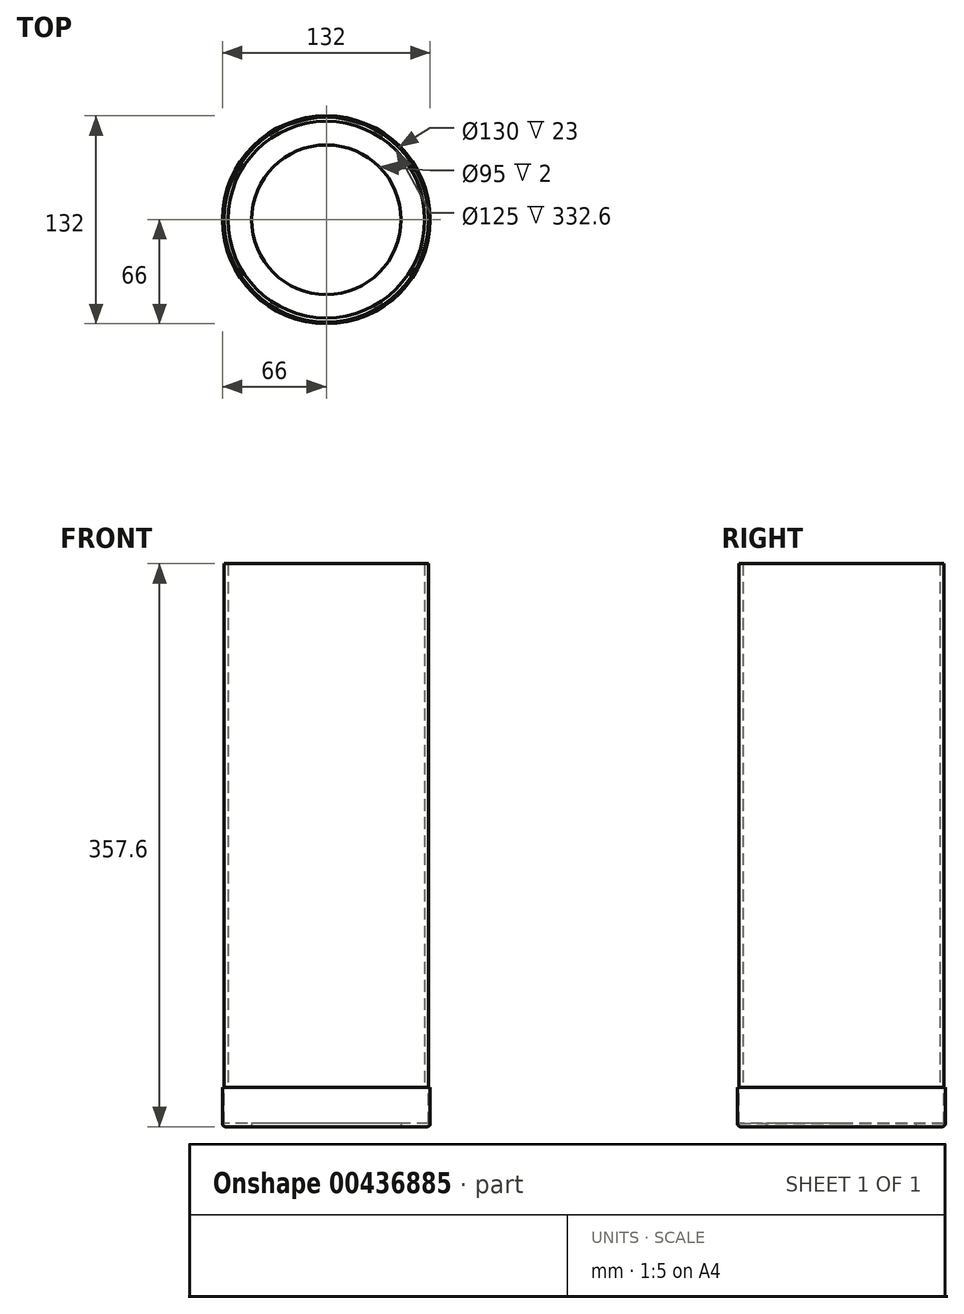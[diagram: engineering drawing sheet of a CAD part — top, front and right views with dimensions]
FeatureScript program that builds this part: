
annotation { "Feature Type Name" : "Feature", "Feature Type Description" : "" }
export const myFeature = defineFeature(function(context is Context, id is Id, definition is map)
    precondition{}
    {
        {
            var Q0;
            Q0=qCreatedBy(makeId("Top.planeOp"),FACE);
            var sketch = newSketch(context, id + "F0", { "sketchPlane" : qUnion([Q0])});
            skCircle(sketch, "E0", {"center": v(0, 0) * mm, "radius": 65 * mm});
            skSolve(sketch);
        }
        {
            var Q0;
            Q0=makeQuery(id+"F0.imprint","IMPRINT",FACE,{"disambiguationData":[TD([[makeQuery(id+"F0.imprint","IMPRINT",EDGE,{"derivedFrom":sQuery(id+"F0.wireOp",EDGE,"E0")}),1.0]])]});
            extrude(context, id + "F1", {"entities" : qUnion([Q0]), "depth" : 355.6 * mm});
        }
        {
            var Q0;
            Q0=makeQuery(id+"F1.opExtrude","CAP_FACE",FACE,{"disambiguationData":[OSD([sQuery(id+"F0.wireOp",EDGE,"E0")])],"isStart":false});
            shell(context, id + "F2", {"entities" : qUnion([Q0]), "thickness" : 2.5 * mm});
        }
        {
            var Q0;
            {var subQ0=sQuery(id+"F0.wireOp",EDGE,"E0");Q0=makeQuery(id+"F2.opShell","OFFSET_FACE",FACE,{"disambiguationData":[OSD([subQ0]),TDD([makeQuery(id+"F1.opExtrude","CAP_FACE",FACE,{"disambiguationData":[OSD([subQ0])],"isStart":true})])]});}
            extrude(context, id + "F3", {"entities" : qUnion([Q0]), "operationType" : NewBodyOperationType.REMOVE, "oppositeDirection" : true, "depth" : 25 * mm});
        }
        {
            var Q0;
            Q0=qCreatedBy(makeId("Top.planeOp"),FACE);
            cPlane(context, id + "F4", {"entities" : qUnion([Q0]), "cplaneType" : CPlaneType.OFFSET, "offset" : 2 * mm, "oppositeDirection" : true, "width" : 150 * mm, "height" : 150 * mm});
        }
        {
            var Q0;
            Q0=qCreatedBy(id+"F4.planeOp",FACE);
            var sketch = newSketch(context, id + "F5", { "sketchPlane" : qUnion([Q0])});
            skCircle(sketch, "E1", {"center": v(0, 0) * mm, "radius": 66 * mm});
            skSolve(sketch);
        }
        {
            var Q0;
            Q0=makeQuery(id+"F5.imprint","IMPRINT",FACE,{"disambiguationData":[TD([[makeQuery(id+"F5.imprint","IMPRINT",EDGE,{"derivedFrom":sQuery(id+"F5.wireOp",EDGE,"E1")}),1.0]])]});
            extrude(context, id + "F6", {"entities" : qUnion([Q0]), "depth" : 25 * mm});
        }
        {
            var Q0;
            Q0=makeQuery(id+"F6.opExtrude","CAP_FACE",FACE,{"disambiguationData":[OSD([sQuery(id+"F5.wireOp",EDGE,"E1")])],"isStart":false});
            var sketch = newSketch(context, id + "F7", { "sketchPlane" : qUnion([Q0])});
            skCircle(sketch, "E2", {"center": v(0, 0) * mm, "radius": 65 * mm});
            skSolve(sketch);
        }
        {
            var Q0;
            Q0=makeQuery(id+"F7.imprint","IMPRINT",FACE,{"disambiguationData":[TD([[makeQuery(id+"F7.imprint","IMPRINT",EDGE,{"derivedFrom":sQuery(id+"F7.wireOp",EDGE,"E2")}),1.0]])]});
            extrude(context, id + "F8", {"entities" : qUnion([Q0]), "operationType" : NewBodyOperationType.REMOVE, "oppositeDirection" : true, "depth" : 23 * mm});
        }
        {
            var Q0;
            Q0=makeQuery(id+"F6.opExtrude","CAP_EDGE",EDGE,{"disambiguationData":[OSD([sQuery(id+"F5.wireOp",EDGE,"E1")])],"isStart":true});
            fillet(context, id + "F9", {"entities" : qUnion([Q0]), "radius" : 2 * mm, "tangentPropagation" : true, "allowEdgeOverflow" : false});
        }
        {
            var Q0;
            Q0=makeQuery(id+"F6.opExtrude","CAP_FACE",FACE,{"disambiguationData":[OSD([sQuery(id+"F5.wireOp",EDGE,"E1")])],"isStart":true});
            var sketch = newSketch(context, id + "F10", { "sketchPlane" : qUnion([Q0])});
            skPoint(sketch, "E3", {"position": v(0, 0) * mm});
            skSolve(sketch);
        }
        {
            var Q0;
            Q0=sQuery(id+"F10.wireOp",VERTEX,"E3");
            var Q1;
            Q1=makeQuery(id+"F6.opExtrude","SWEPT_BODY",BODY,{"disambiguationData":[OSD([sQuery(id+"F5.wireOp",EDGE,"E1")])]});
            hole(context, id + "F11", {"style" : HoleStyle.SIMPLE, "endStyle" : HoleEndStyle.BLIND, "holeDiameter" : 95 * mm, "holeDepth" : 50.8 * mm, "isTappedThrough" : true, "tappedDepth" : 12 * mm, "tapClearance" : 3, "locations" : qUnion([Q0]), "scope" : qUnion([Q1])});
        }
    });
